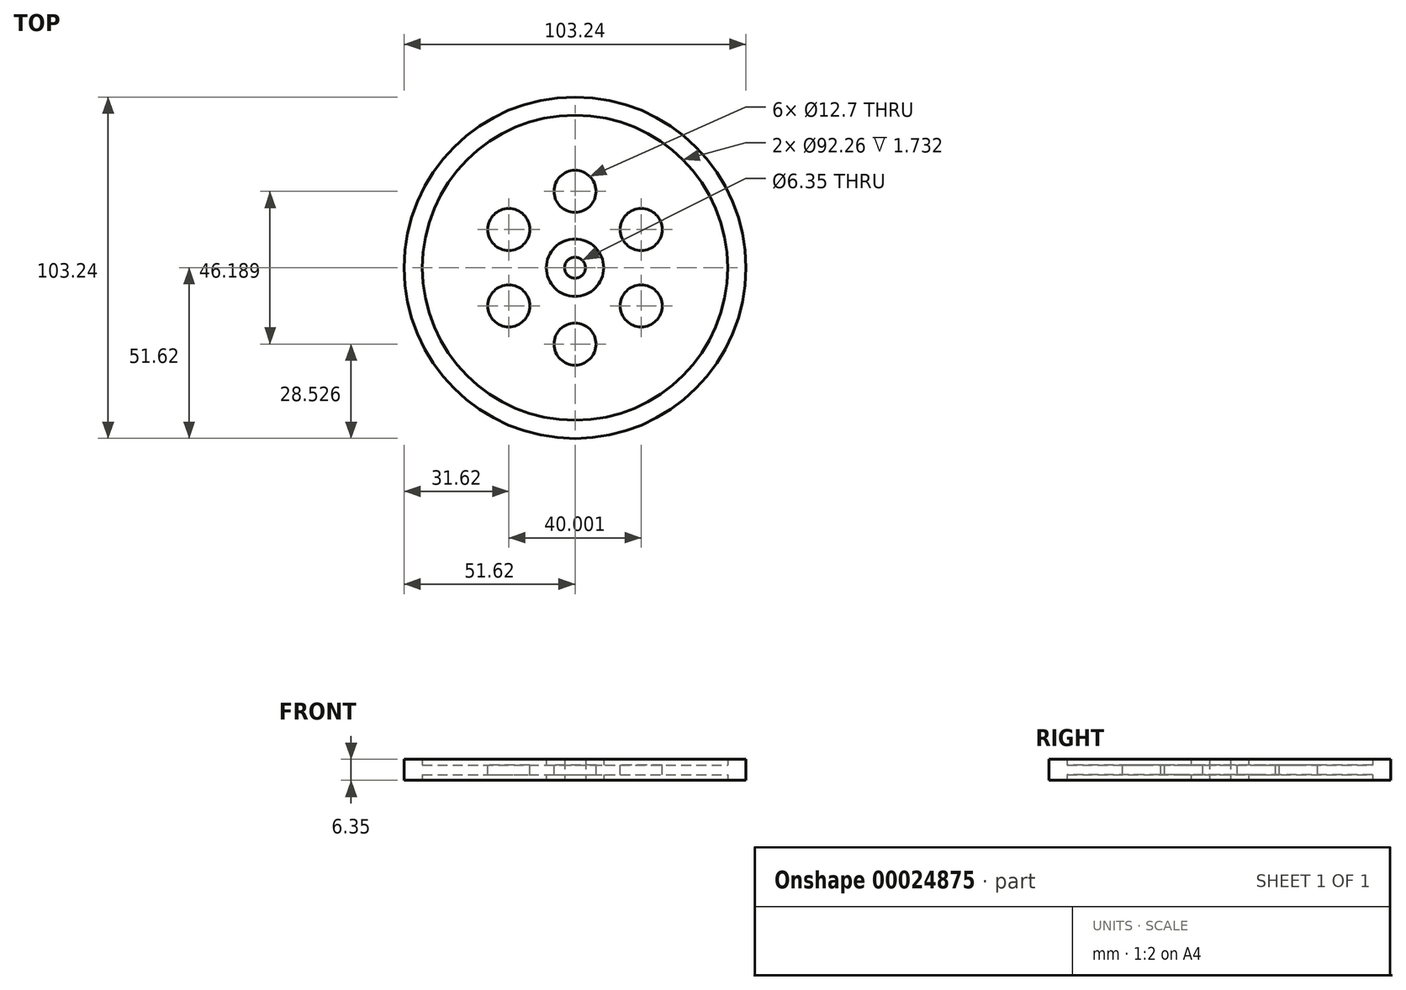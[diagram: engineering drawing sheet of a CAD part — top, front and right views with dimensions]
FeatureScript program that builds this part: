
annotation { "Feature Type Name" : "Feature", "Feature Type Description" : "" }
export const myFeature = defineFeature(function(context is Context, id is Id, definition is map)
    precondition{}
    {
        {
            var Q0;
            Q0=qCreatedBy(makeId("Front.planeOp"),FACE);
            var sketch = newSketch(context, id + "F0", { "sketchPlane" : qUnion([Q0])});
            skLineSegment(sketch, "E0", {"start": v(0, 0) * mm, "end": v(0, 76.27) * mm});
            skLineSegment(sketch, "E1", {"start": v(0, 0) * mm, "end": v(3.18, 0) * mm});
            skLineSegment(sketch, "E2", {"start": v(3.18, 0) * mm, "end": v(3.18, 6.35) * mm});
            skLineSegment(sketch, "E3", {"start": v(3.18, 6.35) * mm, "end": v(8.67, 6.35) * mm});
            skLineSegment(sketch, "E4", {"start": v(8.67, 6.35) * mm, "end": v(8.67, 1.73) * mm});
            skLineSegment(sketch, "E5", {"start": v(8.67, 1.73) * mm, "end": v(46.13, 1.73) * mm});
            skLineSegment(sketch, "E6", {"start": v(46.13, 1.73) * mm, "end": v(46.13, 6.35) * mm});
            skLineSegment(sketch, "E7", {"start": v(46.13, 6.35) * mm, "end": v(51.62, 6.35) * mm});
            skLineSegment(sketch, "E8", {"start": v(51.62, 6.35) * mm, "end": v(51.62, 0) * mm});
            skLineSegment(sketch, "E9", {"start": v(51.62, 0) * mm, "end": v(46.13, 0) * mm});
            skLineSegment(sketch, "E10", {"start": v(46.13, 0) * mm, "end": v(46.13, 4.62) * mm});
            skLineSegment(sketch, "E11", {"start": v(46.13, 4.62) * mm, "end": v(8.67, 4.62) * mm});
            skLineSegment(sketch, "E12", {"start": v(8.67, 4.62) * mm, "end": v(8.67, 0) * mm});
            skLineSegment(sketch, "E13", {"start": v(8.67, 0) * mm, "end": v(3.18, 0) * mm});
            skSolve(sketch);
        }
        {
            var Q0;
            Q0=makeQuery(id+"F0.imprint","IMPRINT",FACE,{"disambiguationData":[TD([[makeQuery(id+"F0.imprint","IMPRINT",EDGE,{"derivedFrom":sQuery(id+"F0.wireOp",EDGE,"E2")}),-1.0]])]});
            var Q1;
            {var subQ1=sQuery(id+"F0.wireOp",EDGE,"E5");Q1=makeQuery(id+"F0.imprint","IMPRINT",FACE,{"disambiguationData":[TD([[makeQuery(id+"F0.imprint","IMPRINT",EDGE,{"derivedFrom":subQ1}),1.0]])]});}
            var Q2;
            {var subQ1=sQuery(id+"F0.wireOp",EDGE,"E6");Q2=makeQuery(id+"F0.imprint","IMPRINT",FACE,{"disambiguationData":[TD([[makeQuery(id+"F0.imprint","IMPRINT",EDGE,{"derivedFrom":subQ1}),-1.0]])]});}
            var Q3;
            Q3=sQuery(id+"F0.wireOp",EDGE,"E0");
            revolve(context, id + "F1", {"entities" : qUnion([Q0, Q1, Q2]), "axis" : qUnion([Q3]), "revolveType" : RevolveType.FULL});
        }
        {
            var Q0;
            Q0=makeQuery(id+"F1.opRevolve","SWEPT_FACE",FACE,{"disambiguationData":[OSD([sQuery(id+"F0.wireOp",EDGE,"E11")])]});
            var sketch = newSketch(context, id + "F2", { "sketchPlane" : qUnion([Q0])});
            skLineSegment(sketch, "E14", {"start": v(0, -8.67) * mm, "end": v(0, -16.74) * mm});
            skCircle(sketch, "E15", {"center": v(0, -23.1) * mm, "radius": 6.35 * mm});
            skCircle(sketch, "E16.1.0", {"center": v(20, 11.55) * mm, "radius": 6.35 * mm});
            skCircle(sketch, "E16.2.0", {"center": v(-20, 11.55) * mm, "radius": 6.35 * mm});
            skPoint(sketch, "E16.center", {"position": v(0, 0) * mm});
            skLineSegment(sketch, "E17", {"start": v(0, 8.67) * mm, "end": v(0, 16.74) * mm});
            skCircle(sketch, "E18", {"center": v(0, 23.1) * mm, "radius": 6.35 * mm});
            skCircle(sketch, "E19.1.0", {"center": v(-20, -11.55) * mm, "radius": 6.35 * mm});
            skCircle(sketch, "E19.2.0", {"center": v(20, -11.55) * mm, "radius": 6.35 * mm});
            skSolve(sketch);
        }
        {
            var Q0;
            Q0=makeQuery(id+"F2.imprint","IMPRINT",FACE,{"disambiguationData":[TD([[makeQuery(id+"F2.imprint","IMPRINT",EDGE,{"derivedFrom":sQuery(id+"F2.wireOp",EDGE,"E19.1.0")}),1.0]])]});
            var Q1;
            Q1=makeQuery(id+"F2.imprint","IMPRINT",FACE,{"disambiguationData":[TD([[makeQuery(id+"F2.imprint","IMPRINT",EDGE,{"derivedFrom":sQuery(id+"F2.wireOp",EDGE,"E15")}),1.0]])]});
            var Q2;
            Q2=makeQuery(id+"F2.imprint","IMPRINT",FACE,{"disambiguationData":[TD([[makeQuery(id+"F2.imprint","IMPRINT",EDGE,{"derivedFrom":sQuery(id+"F2.wireOp",EDGE,"E19.2.0")}),1.0]])]});
            var Q3;
            Q3=makeQuery(id+"F2.imprint","IMPRINT",FACE,{"disambiguationData":[TD([[makeQuery(id+"F2.imprint","IMPRINT",EDGE,{"derivedFrom":sQuery(id+"F2.wireOp",EDGE,"E16.2.0")}),1.0]])]});
            var Q4;
            Q4=makeQuery(id+"F2.imprint","IMPRINT",FACE,{"disambiguationData":[TD([[makeQuery(id+"F2.imprint","IMPRINT",EDGE,{"derivedFrom":sQuery(id+"F2.wireOp",EDGE,"E18")}),1.0]])]});
            var Q5;
            Q5=makeQuery(id+"F2.imprint","IMPRINT",FACE,{"disambiguationData":[TD([[makeQuery(id+"F2.imprint","IMPRINT",EDGE,{"derivedFrom":sQuery(id+"F2.wireOp",EDGE,"E16.1.0")}),1.0]])]});
            var Q6;
            Q6=sQuery(id+"F2.wireOp",EDGE,"E16.1.0");
            var Q7;
            Q7=sQuery(id+"F2.wireOp",EDGE,"E18");
            var Q8;
            Q8=sQuery(id+"F2.wireOp",EDGE,"E16.2.0");
            var Q9;
            Q9=sQuery(id+"F2.wireOp",EDGE,"E19.2.0");
            var Q10;
            Q10=sQuery(id+"F2.wireOp",EDGE,"E15");
            var Q11;
            Q11=sQuery(id+"F2.wireOp",EDGE,"E19.1.0");
            extrude(context, id + "F3", {"entities" : qUnion([Q0, Q1, Q2, Q3, Q4, Q5]), "operationType" : NewBodyOperationType.REMOVE, "surfaceEntities" : qUnion([Q6, Q7, Q8, Q9, Q10, Q11]), "endBound" : BoundingType.SYMMETRIC, "oppositeDirection" : true, "depth" : 25.4 * mm});
        }
    });
